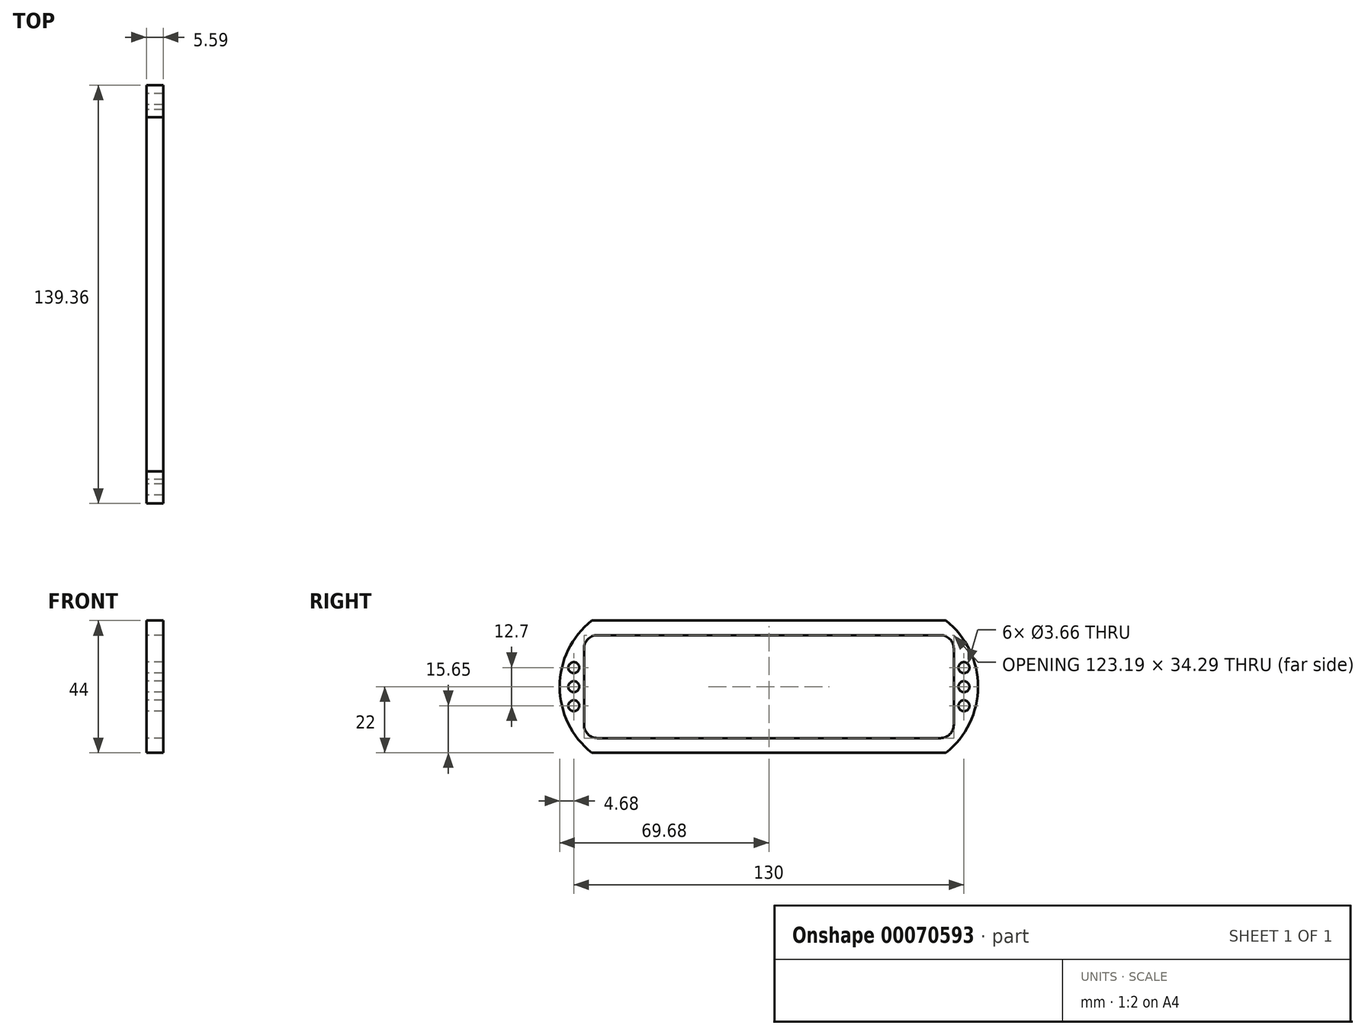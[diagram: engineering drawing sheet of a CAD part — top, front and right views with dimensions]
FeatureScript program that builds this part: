
annotation { "Feature Type Name" : "Feature", "Feature Type Description" : "" }
export const myFeature = defineFeature(function(context is Context, id is Id, definition is map)
    precondition{}
    {
        {
            var Q0;
            Q0=qCreatedBy(makeId("Right.planeOp"),FACE);
            var sketch = newSketch(context, id + "F0", { "sketchPlane" : qUnion([Q0])});
            skLineSegment(sketch, "E0.rect.bottom", {"start": v(59, 22) * mm, "end": v(-59, 22) * mm});
            skLineSegment(sketch, "E0.rect.top", {"start": v(59, -22) * mm, "end": v(-59, -22) * mm});
            skLineSegment(sketch, "E0.rect.left", {"start": v(59, 22) * mm, "end": v(59, -22) * mm, "construction": true});
            skLineSegment(sketch, "E0.rect.right", {"start": v(-59, 22) * mm, "end": v(-59, -22) * mm, "construction": true});
            skPoint(sketch, "E0.rect.middle", {"position": v(0, 0) * mm});
            skLineSegment(sketch, "E1", {"start": v(-59, 0) * mm, "end": v(59, 0) * mm, "construction": true});
            skArc(sketch, "E2", {"start": v(-59, 22) * mm, "mid": v(-69.68, 0) * mm, "end": v(-59, -22) * mm});
            skArc(sketch, "E3", {"start": v(59, -22) * mm, "mid": v(69.68, 0) * mm, "end": v(59, 22) * mm});
            skLineSegment(sketch, "E4.0", {"start": v(61.6, 17.14) * mm, "end": v(-61.6, 17.15) * mm});
            skLineSegment(sketch, "E4.2", {"start": v(61.6, -17.15) * mm, "end": v(-61.6, -17.14) * mm});
            skLineSegment(sketch, "E5.0", {"start": v(-61.6, 17.14) * mm, "end": v(-61.6, -17.14) * mm});
            skLineSegment(sketch, "E6.0", {"start": v(61.6, 17.15) * mm, "end": v(61.6, -17.15) * mm});
            skCircle(sketch, "E7", {"center": v(-65, 0) * mm, "radius": 1.83 * mm});
            skCircle(sketch, "E8", {"center": v(65, 0) * mm, "radius": 1.83 * mm});
            skLineSegment(sketch, "E9", {"start": v(-61.6, 17.14) * mm, "end": v(61.6, -17.15) * mm, "construction": true});
            skCircle(sketch, "E10", {"center": v(-65, 6.35) * mm, "radius": 1.83 * mm});
            skCircle(sketch, "E11", {"center": v(65, 6.35) * mm, "radius": 1.83 * mm});
            skCircle(sketch, "E12", {"center": v(65, -6.35) * mm, "radius": 1.83 * mm});
            skCircle(sketch, "E13", {"center": v(-65, -6.35) * mm, "radius": 1.83 * mm});
            skLineSegment(sketch, "E14", {"start": v(-65, 6.35) * mm, "end": v(-65, -6.35) * mm, "construction": true});
            skSolve(sketch);
        }
        {
            var Q0;
            Q0=makeQuery(id+"F0.imprint","IMPRINT",FACE,{"disambiguationData":[TD([[makeQuery(id+"F0.imprint","IMPRINT",EDGE,{"derivedFrom":sQuery(id+"F0.wireOp",EDGE,"E0.rect.bottom")}),1.0]])]});
            extrude(context, id + "F1", {"entities" : qUnion([Q0]), "depth" : 5.6 * mm});
        }
        {
            var Q0;
            Q0=makeQuery(id+"F1.opExtrude","SWEPT_EDGE",EDGE,{"disambiguationData":[OSD([sQuery(id+"F0.wireOp",EDGE,"E4.0"),sQuery(id+"F0.wireOp",EDGE,"E5.0")])]});
            var Q1;
            Q1=makeQuery(id+"F1.opExtrude","SWEPT_EDGE",EDGE,{"disambiguationData":[OSD([sQuery(id+"F0.wireOp",EDGE,"E4.2"),sQuery(id+"F0.wireOp",EDGE,"E5.0")])]});
            var Q2;
            Q2=makeQuery(id+"F1.opExtrude","SWEPT_EDGE",EDGE,{"disambiguationData":[OSD([sQuery(id+"F0.wireOp",EDGE,"E4.2"),sQuery(id+"F0.wireOp",EDGE,"E6.0")])]});
            var Q3;
            Q3=makeQuery(id+"F1.opExtrude","SWEPT_EDGE",EDGE,{"disambiguationData":[OSD([sQuery(id+"F0.wireOp",EDGE,"E4.0"),sQuery(id+"F0.wireOp",EDGE,"E6.0")])]});
            fillet(context, id + "F2", {"entities" : qUnion([Q0, Q1, Q2, Q3]), "radius" : 4.44 * mm, "tangentPropagation" : true, "allowEdgeOverflow" : false});
        }
    });
